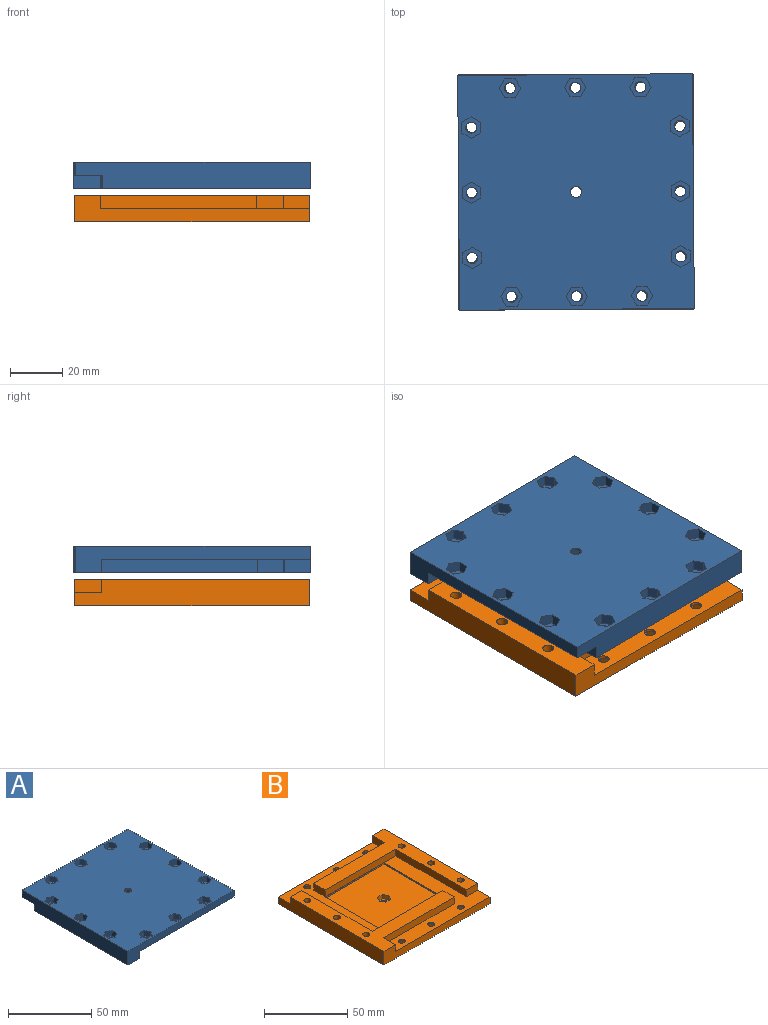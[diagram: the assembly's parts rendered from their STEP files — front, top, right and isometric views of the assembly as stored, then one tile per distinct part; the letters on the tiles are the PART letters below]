
ASSEMBLY  parts=2 mates=1
PART A: 129 faces, bbox 90x90x10 mm
  f0: plane 50x1mm, normal (0,1,0), area 50mm2, adj f19,f20,f21,f24
  f1: plane 50x1mm, normal (0,-1,0), area 50mm2, adj f19,f20,f21,f24
  f2: plane 90x10mm, normal (1,0,0), area 849mm2, adj f3,f4,f6,f21,f22,f123
  f3: plane 90x10mm, normal (0,-1,0), area 499mm2, adj f2,f5,f6,f21,f23,f122
  f4: plane 79.8x69.8mm, normal (0,0,-1), area 1316.5mm2, adj f2,f10,f11,f12,f22,f123,f124,f125
  f5: plane 79.8x69.8mm, normal (0,0,-1), area 1316.5mm2, adj f3,f7,f8,f9,f23,f117,f118,f119
  f6: plane 90x90mm, normal (0,0,1), area 7562.3mm2, adj f2,f3,f22,f23,f32,f33,f34,f35
  f7: cylinder r=2.1mm len=6mm, axis (0,0,-1), area 79.2mm2, adj f5,f116
  f8: cylinder r=2.1mm len=6mm, axis (0,0,-1), area 79.2mm2, adj f5,f109
  f9: cylinder r=2.1mm len=6mm, axis (0,0,-1), area 79.2mm2, adj f5,f102
  f10: cylinder r=2.1mm len=6mm, axis (0,0,-1), area 79.2mm2, adj f4,f95
  f11: cylinder r=2.1mm len=6mm, axis (0,0,-1), area 79.2mm2, adj f4,f88
  f12: cylinder r=2.1mm len=6mm, axis (0,0,-1), area 79.2mm2, adj f4,f81
  f13: cylinder r=2.1mm len=4.2mm, axis (0,0,-1), area 13.2mm2, adj f21,f74
  f14: cylinder r=2.1mm len=4.2mm, axis (0,0,-1), area 13.2mm2, adj f21,f67
  f15: cylinder r=2.1mm len=4.2mm, axis (0,0,-1), area 13.2mm2, adj f21,f60
  f16: cylinder r=2.1mm len=4.2mm, axis (0,0,-1), area 13.2mm2, adj f21,f53
  f17: cylinder r=2.1mm len=4.2mm, axis (0,0,-1), area 13.2mm2, adj f21,f46
  f18: cylinder r=2.1mm len=4.2mm, axis (0,0,-1), area 13.2mm2, adj f21,f39
  f19: plane 50x50mm, normal (0,0,-1), area 2456.3mm2, adj f0,f1,f20,f24,f25,f26,f27,f28
  f20: plane 50x1mm, normal (-1,0,0), area 50mm2, adj f0,f1,f19,f21
  f21: plane 90x90mm, normal (0,0,-1), area 2800.8mm2, adj f0,f1,f2,f3,f13,f14,f15,f16
  f22: plane 90x10mm, normal (0,1,0), area 499mm2, adj f2,f4,f6,f21,f23,f128
  f23: plane 90x10mm, normal (-1,0,0), area 849mm2, adj f3,f5,f6,f21,f22,f117
  f24: plane 50x1mm, normal (1,0,0), area 50mm2, adj f0,f1,f19,f21
  f25: plane 3.55x3mm, normal (-0.87,0.5,0), area 12.3mm2, adj f19,f26,f30,f31
  f26: plane 3.55x3mm, normal (-0.87,-0.5,0), area 12.3mm2, adj f19,f25,f27,f31
  f27: plane 4.1x3mm, normal (0,-1,0), area 12.3mm2, adj f19,f26,f28,f31
  f28: plane 3.55x3mm, normal (0.87,-0.5,0), area 12.3mm2, adj f19,f27,f29,f31
  f29: plane 3.55x3mm, normal (0.87,0.5,0), area 12.3mm2, adj f19,f28,f30,f31
  f30: plane 4.1x3mm, normal (0,1,0), area 12.3mm2, adj f19,f25,f29,f31
  f31: plane 8.2x7.1mm, normal (0,0,-1), area 29.8mm2, adj f25,f26,f27,f28,f29,f30,f32
  f32: cylinder r=2.1mm len=4.2mm, axis (0,0,-1), area 13.2mm2, adj f6,f31
  f33: plane 4x3.55mm, normal (0.87,-0.5,0), area 16.4mm2, adj f6,f34,f38,f39
  f34: plane 4.1x4mm, normal (0,-1,0), area 16.4mm2, adj f6,f33,f35,f39
  f35: plane 4x3.55mm, normal (-0.87,-0.5,0), area 16.4mm2, adj f6,f34,f36,f39
  f36: plane 4x3.55mm, normal (-0.87,0.5,0), area 16.4mm2, adj f6,f35,f37,f39
  f37: plane 4.1x4mm, normal (0,1,0), area 16.4mm2, adj f6,f36,f38,f39
  f38: plane 4x3.55mm, normal (0.87,0.5,0), area 16.4mm2, adj f6,f33,f37,f39
  f39: plane 8.2x7.1mm, normal (0,0,1), area 29.8mm2, adj f18,f33,f34,f35,f36,f37,f38
  f40: plane 4x3.55mm, normal (-0.87,0.5,0), area 16.4mm2, adj f6,f41,f45,f46
  f41: plane 4.1x4mm, normal (0,1,0), area 16.4mm2, adj f6,f40,f42,f46
  f42: plane 4x3.55mm, normal (0.87,0.5,0), area 16.4mm2, adj f6,f41,f43,f46
  f43: plane 4x3.55mm, normal (0.87,-0.5,0), area 16.4mm2, adj f6,f42,f44,f46
  f44: plane 4.1x4mm, normal (0,-1,0), area 16.4mm2, adj f6,f43,f45,f46
  f45: plane 4x3.55mm, normal (-0.87,-0.5,0), area 16.4mm2, adj f6,f40,f44,f46
  f46: plane 8.2x7.1mm, normal (0,0,1), area 29.8mm2, adj f17,f40,f41,f42,f43,f44,f45
  f47: plane 4x3.55mm, normal (-0.87,0.5,0), area 16.4mm2, adj f6,f48,f52,f53
  f48: plane 4.1x4mm, normal (0,1,0), area 16.4mm2, adj f6,f47,f49,f53
  f49: plane 4x3.55mm, normal (0.87,0.5,0), area 16.4mm2, adj f6,f48,f50,f53
  f50: plane 4x3.55mm, normal (0.87,-0.5,0), area 16.4mm2, adj f6,f49,f51,f53
  f51: plane 4.1x4mm, normal (0,-1,0), area 16.4mm2, adj f6,f50,f52,f53
  f52: plane 4x3.55mm, normal (-0.87,-0.5,0), area 16.4mm2, adj f6,f47,f51,f53
  f53: plane 8.2x7.1mm, normal (0,0,1), area 29.8mm2, adj f16,f47,f48,f49,f50,f51,f52
  f54: plane 4x3.55mm, normal (-0.87,-0.5,0), area 16.4mm2, adj f6,f55,f59,f60
  f55: plane 4x3.55mm, normal (-0.87,0.5,0), area 16.4mm2, adj f6,f54,f56,f60
  f56: plane 4.1x4mm, normal (0,1,0), area 16.4mm2, adj f6,f55,f57,f60
  f57: plane 4x3.55mm, normal (0.87,0.5,0), area 16.4mm2, adj f6,f56,f58,f60
  f58: plane 4x3.55mm, normal (0.87,-0.5,0), area 16.4mm2, adj f6,f57,f59,f60
  f59: plane 4.1x4mm, normal (0,-1,0), area 16.4mm2, adj f6,f54,f58,f60
  f60: plane 8.2x7.1mm, normal (0,0,1), area 29.8mm2, adj f15,f54,f55,f56,f57,f58,f59
  f61: plane 4x3.55mm, normal (0.87,-0.5,0), area 16.4mm2, adj f6,f62,f66,f67
  f62: plane 4.1x4mm, normal (0,-1,0), area 16.4mm2, adj f6,f61,f63,f67
  f63: plane 4x3.55mm, normal (-0.87,-0.5,0), area 16.4mm2, adj f6,f62,f64,f67
  f64: plane 4x3.55mm, normal (-0.87,0.5,0), area 16.4mm2, adj f6,f63,f65,f67
  f65: plane 4.1x4mm, normal (0,1,0), area 16.4mm2, adj f6,f64,f66,f67
  f66: plane 4x3.55mm, normal (0.87,0.5,0), area 16.4mm2, adj f6,f61,f65,f67
  f67: plane 8.2x7.1mm, normal (0,0,1), area 29.8mm2, adj f14,f61,f62,f63,f64,f65,f66
  f68: plane 4x3.55mm, normal (-0.87,-0.5,0), area 16.4mm2, adj f6,f69,f73,f74
  f69: plane 4x3.55mm, normal (-0.87,0.5,0), area 16.4mm2, adj f6,f68,f70,f74
  f70: plane 4.1x4mm, normal (0,1,0), area 16.4mm2, adj f6,f69,f71,f74
  f71: plane 4x3.55mm, normal (0.87,0.5,0), area 16.4mm2, adj f6,f70,f72,f74
  f72: plane 4x3.55mm, normal (0.87,-0.5,0), area 16.4mm2, adj f6,f71,f73,f74
  f73: plane 4.1x4mm, normal (0,-1,0), area 16.4mm2, adj f6,f68,f72,f74
  f74: plane 8.2x7.1mm, normal (0,0,1), area 29.8mm2, adj f13,f68,f69,f70,f71,f72,f73
  f75: plane 4x3.55mm, normal (-0.5,0.87,0), area 16.4mm2, adj f6,f76,f80,f81
  f76: plane 4x3.55mm, normal (0.5,0.87,0), area 16.4mm2, adj f6,f75,f77,f81
  f77: plane 4.1x4mm, normal (1,0,0), area 16.4mm2, adj f6,f76,f78,f81
  f78: plane 4x3.55mm, normal (0.5,-0.87,0), area 16.4mm2, adj f6,f77,f79,f81
  f79: plane 4x3.55mm, normal (-0.5,-0.87,0), area 16.4mm2, adj f6,f78,f80,f81
  f80: plane 4.1x4mm, normal (-1,0,0), area 16.4mm2, adj f6,f75,f79,f81
  f81: plane 8.2x7.1mm, normal (0,0,1), area 29.8mm2, adj f12,f75,f76,f77,f78,f79,f80
  f82: plane 4x3.55mm, normal (0.5,0.87,0), area 16.4mm2, adj f6,f83,f87,f88
  f83: plane 4.1x4mm, normal (1,0,0), area 16.4mm2, adj f6,f82,f84,f88
  f84: plane 4x3.55mm, normal (0.5,-0.87,0), area 16.4mm2, adj f6,f83,f85,f88
  f85: plane 4x3.55mm, normal (-0.5,-0.87,0), area 16.4mm2, adj f6,f84,f86,f88
  f86: plane 4.1x4mm, normal (-1,0,0), area 16.4mm2, adj f6,f85,f87,f88
  f87: plane 4x3.55mm, normal (-0.5,0.87,0), area 16.4mm2, adj f6,f82,f86,f88
  f88: plane 8.2x7.1mm, normal (0,0,1), area 29.8mm2, adj f11,f82,f83,f84,f85,f86,f87
  f89: plane 4x3.55mm, normal (0.5,0.87,0), area 16.4mm2, adj f6,f90,f94,f95
  f90: plane 4.1x4mm, normal (1,0,0), area 16.4mm2, adj f6,f89,f91,f95
  f91: plane 4x3.55mm, normal (0.5,-0.87,0), area 16.4mm2, adj f6,f90,f92,f95
  f92: plane 4x3.55mm, normal (-0.5,-0.87,0), area 16.4mm2, adj f6,f91,f93,f95
  f93: plane 4.1x4mm, normal (-1,0,0), area 16.4mm2, adj f6,f92,f94,f95
  f94: plane 4x3.55mm, normal (-0.5,0.87,0), area 16.4mm2, adj f6,f89,f93,f95
  f95: plane 8.2x7.1mm, normal (0,0,1), area 29.8mm2, adj f10,f89,f90,f91,f92,f93,f94
  f96: plane 4x3.55mm, normal (-0.5,-0.87,0), area 16.4mm2, adj f6,f97,f101,f102
  f97: plane 4.1x4mm, normal (-1,0,0), area 16.4mm2, adj f6,f96,f98,f102
  f98: plane 4x3.55mm, normal (-0.5,0.87,0), area 16.4mm2, adj f6,f97,f99,f102
  f99: plane 4x3.55mm, normal (0.5,0.87,0), area 16.4mm2, adj f6,f98,f100,f102
  f100: plane 4.1x4mm, normal (1,0,0), area 16.4mm2, adj f6,f99,f101,f102
  f101: plane 4x3.55mm, normal (0.5,-0.87,0), area 16.4mm2, adj f6,f96,f100,f102
  f102: plane 8.2x7.1mm, normal (0,0,1), area 29.8mm2, adj f9,f96,f97,f98,f99,f100,f101
  f103: plane 4x3.55mm, normal (-0.5,-0.87,0), area 16.4mm2, adj f6,f104,f108,f109
  f104: plane 4.1x4mm, normal (-1,0,0), area 16.4mm2, adj f6,f103,f105,f109
  f105: plane 4x3.55mm, normal (-0.5,0.87,0), area 16.4mm2, adj f6,f104,f106,f109
  f106: plane 4x3.55mm, normal (0.5,0.87,0), area 16.4mm2, adj f6,f105,f107,f109
  f107: plane 4.1x4mm, normal (1,0,0), area 16.4mm2, adj f6,f106,f108,f109
  f108: plane 4x3.55mm, normal (0.5,-0.87,0), area 16.4mm2, adj f6,f103,f107,f109
  f109: plane 8.2x7.1mm, normal (0,0,1), area 29.8mm2, adj f8,f103,f104,f105,f106,f107,f108
  f110: plane 4x3.55mm, normal (0.5,0.87,0), area 16.4mm2, adj f6,f111,f115,f116
  f111: plane 4.1x4mm, normal (1,0,0), area 16.4mm2, adj f6,f110,f112,f116
  f112: plane 4x3.55mm, normal (0.5,-0.87,0), area 16.4mm2, adj f6,f111,f113,f116
  f113: plane 4x3.55mm, normal (-0.5,-0.87,0), area 16.4mm2, adj f6,f112,f114,f116
  f114: plane 4.1x4mm, normal (-1,0,0), area 16.4mm2, adj f6,f113,f115,f116
  f115: plane 4x3.55mm, normal (-0.5,0.87,0), area 16.4mm2, adj f6,f110,f114,f116
  f116: plane 8.2x7.1mm, normal (0,0,1), area 29.8mm2, adj f7,f110,f111,f112,f113,f114,f115
  f117: plane 9.8x5mm, normal (0,1,0), area 49mm2, adj f5,f21,f23,f118
  f118: plane 60x5mm, normal (1,0,0), area 300mm2, adj f5,f21,f117,f119
  f119: plane 60x5mm, normal (0,1,0), area 300mm2, adj f5,f21,f118,f120
  f120: plane 9.6x5mm, normal (1,0,0), area 48mm2, adj f5,f21,f119,f121
  f121: plane 60x5mm, normal (0,-1,0), area 300mm2, adj f5,f21,f120,f122
  f122: plane 10.2x5mm, normal (1,0,0), area 51mm2, adj f3,f5,f21,f121
  f123: plane 9.8x5mm, normal (0,-1,0), area 49mm2, adj f2,f4,f21,f124
  f124: plane 60x5mm, normal (-1,0,0), area 300mm2, adj f4,f21,f123,f125
  f125: plane 60x5mm, normal (0,-1,0), area 300mm2, adj f4,f21,f124,f126
  f126: plane 9.6x5mm, normal (-1,0,0), area 48mm2, adj f4,f21,f125,f127
  f127: plane 60x5mm, normal (0,1,0), area 300mm2, adj f4,f21,f126,f128
  f128: plane 10.2x5mm, normal (-1,0,0), area 51mm2, adj f4,f21,f22,f127
PART B: 129 faces, bbox 90x90x10 mm
  f0: plane 50x1mm, normal (0,1,0), area 50mm2, adj f19,f20,f21,f24
  f1: plane 50x1mm, normal (0,-1,0), area 50mm2, adj f19,f20,f21,f24
  f2: plane 90x10mm, normal (1,0,0), area 849mm2, adj f3,f4,f6,f21,f22,f123
  f3: plane 90x10mm, normal (0,-1,0), area 499mm2, adj f2,f5,f6,f21,f23,f122
  f4: plane 79.8x69.8mm, normal (0,0,1), area 1316.5mm2, adj f2,f10,f11,f12,f22,f123,f124,f125
  f5: plane 79.8x69.8mm, normal (0,0,1), area 1316.5mm2, adj f3,f7,f8,f9,f23,f117,f118,f119
  f6: plane 90x90mm, normal (0,0,-1), area 7562.3mm2, adj f2,f3,f22,f23,f32,f33,f34,f35
  f7: cylinder r=2.1mm len=6mm, axis (0,0,1), area 79.2mm2, adj f5,f116
  f8: cylinder r=2.1mm len=6mm, axis (0,0,1), area 79.2mm2, adj f5,f109
  f9: cylinder r=2.1mm len=6mm, axis (0,0,1), area 79.2mm2, adj f5,f102
  f10: cylinder r=2.1mm len=6mm, axis (0,0,1), area 79.2mm2, adj f4,f95
  f11: cylinder r=2.1mm len=6mm, axis (0,0,1), area 79.2mm2, adj f4,f88
  f12: cylinder r=2.1mm len=6mm, axis (0,0,1), area 79.2mm2, adj f4,f81
  f13: cylinder r=2.1mm len=4.2mm, axis (0,0,1), area 13.2mm2, adj f21,f74
  f14: cylinder r=2.1mm len=4.2mm, axis (0,0,1), area 13.2mm2, adj f21,f67
  f15: cylinder r=2.1mm len=4.2mm, axis (0,0,1), area 13.2mm2, adj f21,f60
  f16: cylinder r=2.1mm len=4.2mm, axis (0,0,1), area 13.2mm2, adj f21,f53
  f17: cylinder r=2.1mm len=4.2mm, axis (0,0,1), area 13.2mm2, adj f21,f46
  f18: cylinder r=2.1mm len=4.2mm, axis (0,0,1), area 13.2mm2, adj f21,f39
  f19: plane 50x50mm, normal (0,0,1), area 2456.3mm2, adj f0,f1,f20,f24,f25,f26,f27,f28
  f20: plane 50x1mm, normal (-1,0,0), area 50mm2, adj f0,f1,f19,f21
  f21: plane 90x90mm, normal (0,0,1), area 2800.8mm2, adj f0,f1,f2,f3,f13,f14,f15,f16
  f22: plane 90x10mm, normal (0,1,0), area 499mm2, adj f2,f4,f6,f21,f23,f128
  f23: plane 90x10mm, normal (-1,0,0), area 849mm2, adj f3,f5,f6,f21,f22,f117
  f24: plane 50x1mm, normal (1,0,0), area 50mm2, adj f0,f1,f19,f21
  f25: plane 3.55x3mm, normal (-0.87,0.5,0), area 12.3mm2, adj f19,f26,f30,f31
  f26: plane 3.55x3mm, normal (-0.87,-0.5,0), area 12.3mm2, adj f19,f25,f27,f31
  f27: plane 4.1x3mm, normal (0,-1,0), area 12.3mm2, adj f19,f26,f28,f31
  f28: plane 3.55x3mm, normal (0.87,-0.5,0), area 12.3mm2, adj f19,f27,f29,f31
  f29: plane 3.55x3mm, normal (0.87,0.5,0), area 12.3mm2, adj f19,f28,f30,f31
  f30: plane 4.1x3mm, normal (0,1,0), area 12.3mm2, adj f19,f25,f29,f31
  f31: plane 8.2x7.1mm, normal (0,0,1), area 29.8mm2, adj f25,f26,f27,f28,f29,f30,f32
  f32: cylinder r=2.1mm len=4.2mm, axis (0,0,1), area 13.2mm2, adj f6,f31
  f33: plane 4x3.55mm, normal (0.87,-0.5,0), area 16.4mm2, adj f6,f34,f38,f39
  f34: plane 4.1x4mm, normal (0,-1,0), area 16.4mm2, adj f6,f33,f35,f39
  f35: plane 4x3.55mm, normal (-0.87,-0.5,0), area 16.4mm2, adj f6,f34,f36,f39
  f36: plane 4x3.55mm, normal (-0.87,0.5,0), area 16.4mm2, adj f6,f35,f37,f39
  f37: plane 4.1x4mm, normal (0,1,0), area 16.4mm2, adj f6,f36,f38,f39
  f38: plane 4x3.55mm, normal (0.87,0.5,0), area 16.4mm2, adj f6,f33,f37,f39
  f39: plane 8.2x7.1mm, normal (0,0,-1), area 29.8mm2, adj f18,f33,f34,f35,f36,f37,f38
  f40: plane 4x3.55mm, normal (-0.87,0.5,0), area 16.4mm2, adj f6,f41,f45,f46
  f41: plane 4.1x4mm, normal (0,1,0), area 16.4mm2, adj f6,f40,f42,f46
  f42: plane 4x3.55mm, normal (0.87,0.5,0), area 16.4mm2, adj f6,f41,f43,f46
  f43: plane 4x3.55mm, normal (0.87,-0.5,0), area 16.4mm2, adj f6,f42,f44,f46
  f44: plane 4.1x4mm, normal (0,-1,0), area 16.4mm2, adj f6,f43,f45,f46
  f45: plane 4x3.55mm, normal (-0.87,-0.5,0), area 16.4mm2, adj f6,f40,f44,f46
  f46: plane 8.2x7.1mm, normal (0,0,-1), area 29.8mm2, adj f17,f40,f41,f42,f43,f44,f45
  f47: plane 4x3.55mm, normal (-0.87,0.5,0), area 16.4mm2, adj f6,f48,f52,f53
  f48: plane 4.1x4mm, normal (0,1,0), area 16.4mm2, adj f6,f47,f49,f53
  f49: plane 4x3.55mm, normal (0.87,0.5,0), area 16.4mm2, adj f6,f48,f50,f53
  f50: plane 4x3.55mm, normal (0.87,-0.5,0), area 16.4mm2, adj f6,f49,f51,f53
  f51: plane 4.1x4mm, normal (0,-1,0), area 16.4mm2, adj f6,f50,f52,f53
  f52: plane 4x3.55mm, normal (-0.87,-0.5,0), area 16.4mm2, adj f6,f47,f51,f53
  f53: plane 8.2x7.1mm, normal (0,0,-1), area 29.8mm2, adj f16,f47,f48,f49,f50,f51,f52
  f54: plane 4x3.55mm, normal (-0.87,-0.5,0), area 16.4mm2, adj f6,f55,f59,f60
  f55: plane 4x3.55mm, normal (-0.87,0.5,0), area 16.4mm2, adj f6,f54,f56,f60
  f56: plane 4.1x4mm, normal (0,1,0), area 16.4mm2, adj f6,f55,f57,f60
  f57: plane 4x3.55mm, normal (0.87,0.5,0), area 16.4mm2, adj f6,f56,f58,f60
  f58: plane 4x3.55mm, normal (0.87,-0.5,0), area 16.4mm2, adj f6,f57,f59,f60
  f59: plane 4.1x4mm, normal (0,-1,0), area 16.4mm2, adj f6,f54,f58,f60
  f60: plane 8.2x7.1mm, normal (0,0,-1), area 29.8mm2, adj f15,f54,f55,f56,f57,f58,f59
  f61: plane 4x3.55mm, normal (0.87,-0.5,0), area 16.4mm2, adj f6,f62,f66,f67
  f62: plane 4.1x4mm, normal (0,-1,0), area 16.4mm2, adj f6,f61,f63,f67
  f63: plane 4x3.55mm, normal (-0.87,-0.5,0), area 16.4mm2, adj f6,f62,f64,f67
  f64: plane 4x3.55mm, normal (-0.87,0.5,0), area 16.4mm2, adj f6,f63,f65,f67
  f65: plane 4.1x4mm, normal (0,1,0), area 16.4mm2, adj f6,f64,f66,f67
  f66: plane 4x3.55mm, normal (0.87,0.5,0), area 16.4mm2, adj f6,f61,f65,f67
  f67: plane 8.2x7.1mm, normal (0,0,-1), area 29.8mm2, adj f14,f61,f62,f63,f64,f65,f66
  f68: plane 4x3.55mm, normal (-0.87,-0.5,0), area 16.4mm2, adj f6,f69,f73,f74
  f69: plane 4x3.55mm, normal (-0.87,0.5,0), area 16.4mm2, adj f6,f68,f70,f74
  f70: plane 4.1x4mm, normal (0,1,0), area 16.4mm2, adj f6,f69,f71,f74
  f71: plane 4x3.55mm, normal (0.87,0.5,0), area 16.4mm2, adj f6,f70,f72,f74
  f72: plane 4x3.55mm, normal (0.87,-0.5,0), area 16.4mm2, adj f6,f71,f73,f74
  f73: plane 4.1x4mm, normal (0,-1,0), area 16.4mm2, adj f6,f68,f72,f74
  f74: plane 8.2x7.1mm, normal (0,0,-1), area 29.8mm2, adj f13,f68,f69,f70,f71,f72,f73
  f75: plane 4x3.55mm, normal (-0.5,0.87,0), area 16.4mm2, adj f6,f76,f80,f81
  f76: plane 4x3.55mm, normal (0.5,0.87,0), area 16.4mm2, adj f6,f75,f77,f81
  f77: plane 4.1x4mm, normal (1,0,0), area 16.4mm2, adj f6,f76,f78,f81
  f78: plane 4x3.55mm, normal (0.5,-0.87,0), area 16.4mm2, adj f6,f77,f79,f81
  f79: plane 4x3.55mm, normal (-0.5,-0.87,0), area 16.4mm2, adj f6,f78,f80,f81
  f80: plane 4.1x4mm, normal (-1,0,0), area 16.4mm2, adj f6,f75,f79,f81
  f81: plane 8.2x7.1mm, normal (0,0,-1), area 29.8mm2, adj f12,f75,f76,f77,f78,f79,f80
  f82: plane 4x3.55mm, normal (0.5,0.87,0), area 16.4mm2, adj f6,f83,f87,f88
  f83: plane 4.1x4mm, normal (1,0,0), area 16.4mm2, adj f6,f82,f84,f88
  f84: plane 4x3.55mm, normal (0.5,-0.87,0), area 16.4mm2, adj f6,f83,f85,f88
  f85: plane 4x3.55mm, normal (-0.5,-0.87,0), area 16.4mm2, adj f6,f84,f86,f88
  f86: plane 4.1x4mm, normal (-1,0,0), area 16.4mm2, adj f6,f85,f87,f88
  f87: plane 4x3.55mm, normal (-0.5,0.87,0), area 16.4mm2, adj f6,f82,f86,f88
  f88: plane 8.2x7.1mm, normal (0,0,-1), area 29.8mm2, adj f11,f82,f83,f84,f85,f86,f87
  f89: plane 4x3.55mm, normal (0.5,0.87,0), area 16.4mm2, adj f6,f90,f94,f95
  f90: plane 4.1x4mm, normal (1,0,0), area 16.4mm2, adj f6,f89,f91,f95
  f91: plane 4x3.55mm, normal (0.5,-0.87,0), area 16.4mm2, adj f6,f90,f92,f95
  f92: plane 4x3.55mm, normal (-0.5,-0.87,0), area 16.4mm2, adj f6,f91,f93,f95
  f93: plane 4.1x4mm, normal (-1,0,0), area 16.4mm2, adj f6,f92,f94,f95
  f94: plane 4x3.55mm, normal (-0.5,0.87,0), area 16.4mm2, adj f6,f89,f93,f95
  f95: plane 8.2x7.1mm, normal (0,0,-1), area 29.8mm2, adj f10,f89,f90,f91,f92,f93,f94
  f96: plane 4x3.55mm, normal (-0.5,-0.87,0), area 16.4mm2, adj f6,f97,f101,f102
  f97: plane 4.1x4mm, normal (-1,0,0), area 16.4mm2, adj f6,f96,f98,f102
  f98: plane 4x3.55mm, normal (-0.5,0.87,0), area 16.4mm2, adj f6,f97,f99,f102
  f99: plane 4x3.55mm, normal (0.5,0.87,0), area 16.4mm2, adj f6,f98,f100,f102
  f100: plane 4.1x4mm, normal (1,0,0), area 16.4mm2, adj f6,f99,f101,f102
  f101: plane 4x3.55mm, normal (0.5,-0.87,0), area 16.4mm2, adj f6,f96,f100,f102
  f102: plane 8.2x7.1mm, normal (0,0,-1), area 29.8mm2, adj f9,f96,f97,f98,f99,f100,f101
  f103: plane 4x3.55mm, normal (-0.5,-0.87,0), area 16.4mm2, adj f6,f104,f108,f109
  f104: plane 4.1x4mm, normal (-1,0,0), area 16.4mm2, adj f6,f103,f105,f109
  f105: plane 4x3.55mm, normal (-0.5,0.87,0), area 16.4mm2, adj f6,f104,f106,f109
  f106: plane 4x3.55mm, normal (0.5,0.87,0), area 16.4mm2, adj f6,f105,f107,f109
  f107: plane 4.1x4mm, normal (1,0,0), area 16.4mm2, adj f6,f106,f108,f109
  f108: plane 4x3.55mm, normal (0.5,-0.87,0), area 16.4mm2, adj f6,f103,f107,f109
  f109: plane 8.2x7.1mm, normal (0,0,-1), area 29.8mm2, adj f8,f103,f104,f105,f106,f107,f108
  f110: plane 4x3.55mm, normal (0.5,0.87,0), area 16.4mm2, adj f6,f111,f115,f116
  f111: plane 4.1x4mm, normal (1,0,0), area 16.4mm2, adj f6,f110,f112,f116
  f112: plane 4x3.55mm, normal (0.5,-0.87,0), area 16.4mm2, adj f6,f111,f113,f116
  f113: plane 4x3.55mm, normal (-0.5,-0.87,0), area 16.4mm2, adj f6,f112,f114,f116
  f114: plane 4.1x4mm, normal (-1,0,0), area 16.4mm2, adj f6,f113,f115,f116
  f115: plane 4x3.55mm, normal (-0.5,0.87,0), area 16.4mm2, adj f6,f110,f114,f116
  f116: plane 8.2x7.1mm, normal (0,0,-1), area 29.8mm2, adj f7,f110,f111,f112,f113,f114,f115
  f117: plane 9.8x5mm, normal (0,1,0), area 49mm2, adj f5,f21,f23,f118
  f118: plane 60x5mm, normal (1,0,0), area 300mm2, adj f5,f21,f117,f119
  f119: plane 60x5mm, normal (0,1,0), area 300mm2, adj f5,f21,f118,f120
  f120: plane 9.6x5mm, normal (1,0,0), area 48mm2, adj f5,f21,f119,f121
  f121: plane 60x5mm, normal (0,-1,0), area 300mm2, adj f5,f21,f120,f122
  f122: plane 10.2x5mm, normal (1,0,0), area 51mm2, adj f3,f5,f21,f121
  f123: plane 9.8x5mm, normal (0,-1,0), area 49mm2, adj f2,f4,f21,f124
  f124: plane 60x5mm, normal (-1,0,0), area 300mm2, adj f4,f21,f123,f125
  f125: plane 60x5mm, normal (0,-1,0), area 300mm2, adj f4,f21,f124,f126
  f126: plane 9.6x5mm, normal (-1,0,0), area 48mm2, adj f4,f21,f125,f127
  f127: plane 60x5mm, normal (0,1,0), area 300mm2, adj f4,f21,f126,f128
  f128: plane 10.2x5mm, normal (-1,0,0), area 51mm2, adj f4,f21,f22,f127
PLACE A rot(axis=(0,0,-1),89.5deg) t=(0,0,3)mm
PLACE B at identity fixed
MATE revolute A.f32 <-> B.f32  axis (0,0,-1) through (0,0,19)mm
